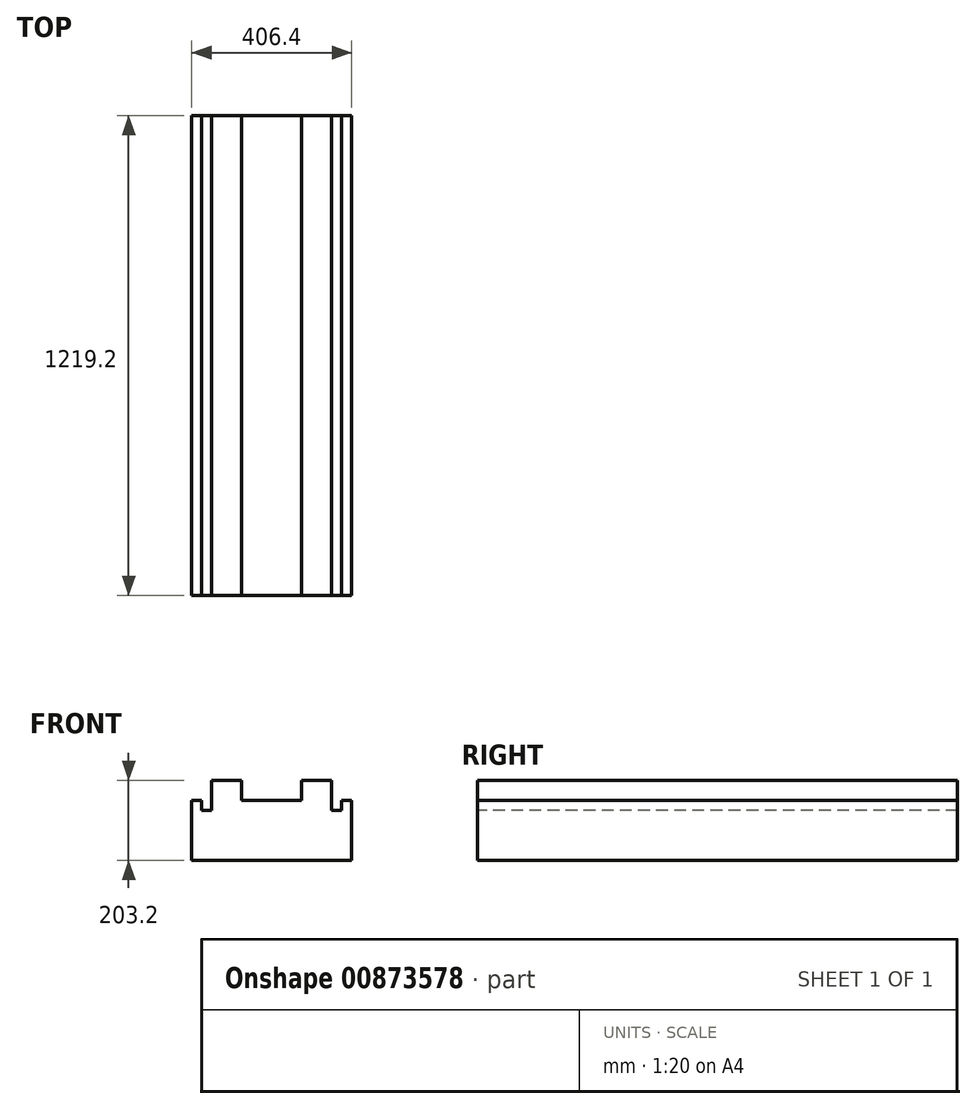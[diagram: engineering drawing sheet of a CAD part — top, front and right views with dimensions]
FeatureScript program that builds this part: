
annotation { "Feature Type Name" : "Feature", "Feature Type Description" : "" }
export const myFeature = defineFeature(function(context is Context, id is Id, definition is map)
    precondition{}
    {
        {
            var Q0;
            Q0=qCreatedBy(makeId("Front.planeOp"),FACE);
            var sketch = newSketch(context, id + "F0", { "sketchPlane" : qUnion([Q0])});
            skLineSegment(sketch, "E0.bottom", {"start": v(-76.2, 101.6) * mm, "end": v(-152.4, 101.6) * mm});
            skLineSegment(sketch, "E0.top", {"start": v(0, -101.6) * mm, "end": v(-203.2, -101.6) * mm});
            skPoint(sketch, "E0.middle", {"position": v(0, 0) * mm});
            skLineSegment(sketch, "E1", {"start": v(-267, 0) * mm, "end": v(337.57, 0) * mm, "construction": true});
            skLineSegment(sketch, "E2", {"start": v(0, 163.2) * mm, "end": v(0, -190.74) * mm, "construction": true});
            skLineSegment(sketch, "E3.top", {"start": v(-177.8, 25.4) * mm, "end": v(-152.4, 25.4) * mm});
            skLineSegment(sketch, "E3.right", {"start": v(-152.4, 101.6) * mm, "end": v(-152.4, 25.4) * mm});
            skPoint(sketch, "E0.left.end.orphan", {"position": v(203.2, -101.6) * mm});
            skLineSegment(sketch, "E4.MirrorCS", {"start": v(152.4, 101.6) * mm, "end": v(152.4, 25.4) * mm});
            skLineSegment(sketch, "E5.MirrorCS", {"start": v(177.8, 25.4) * mm, "end": v(152.4, 25.4) * mm});
            skLineSegment(sketch, "E6.MirrorCS", {"start": v(0, -101.6) * mm, "end": v(203.2, -101.6) * mm});
            skLineSegment(sketch, "E7.MirrorCS", {"start": v(76.2, 101.6) * mm, "end": v(152.4, 101.6) * mm});
            skLineSegment(sketch, "E8.bottom", {"start": v(76.2, 50.8) * mm, "end": v(-76.2, 50.8) * mm});
            skLineSegment(sketch, "E8.left", {"start": v(76.2, 50.8) * mm, "end": v(76.2, 101.6) * mm});
            skLineSegment(sketch, "E8.right", {"start": v(-76.2, 50.8) * mm, "end": v(-76.2, 101.6) * mm});
            skPoint(sketch, "E8.middle", {"position": v(0, 101.6) * mm});
            skLineSegment(sketch, "E9.top", {"start": v(-203.2, 50.8) * mm, "end": v(-177.8, 50.8) * mm});
            skLineSegment(sketch, "E9.right", {"start": v(-177.8, 25.4) * mm, "end": v(-177.8, 50.8) * mm});
            skLineSegment(sketch, "E10.MirrorCS", {"start": v(203.2, 50.8) * mm, "end": v(177.8, 50.8) * mm});
            skLineSegment(sketch, "E11.MirrorCS", {"start": v(177.8, 25.4) * mm, "end": v(177.8, 50.8) * mm});
            skLineSegment(sketch, "E12", {"start": v(-203.2, 50.8) * mm, "end": v(-203.2, -101.6) * mm});
            skPoint(sketch, "E13.MirrorCS.end.orphan", {"position": v(203.2, 50.8) * mm});
            skLineSegment(sketch, "E14", {"start": v(203.2, 50.8) * mm, "end": v(203.2, -101.6) * mm});
            skSolve(sketch);
        }
        {
            var Q0;
            Q0 = qSketchRegion(id + "F0", true);
            extrude(context, id + "F1", {"entities" : qUnion([Q0]), "oppositeDirection" : true, "depth" : 1219.2 * mm, "offsetDistance" : 25.4 * mm});
        }
    });
